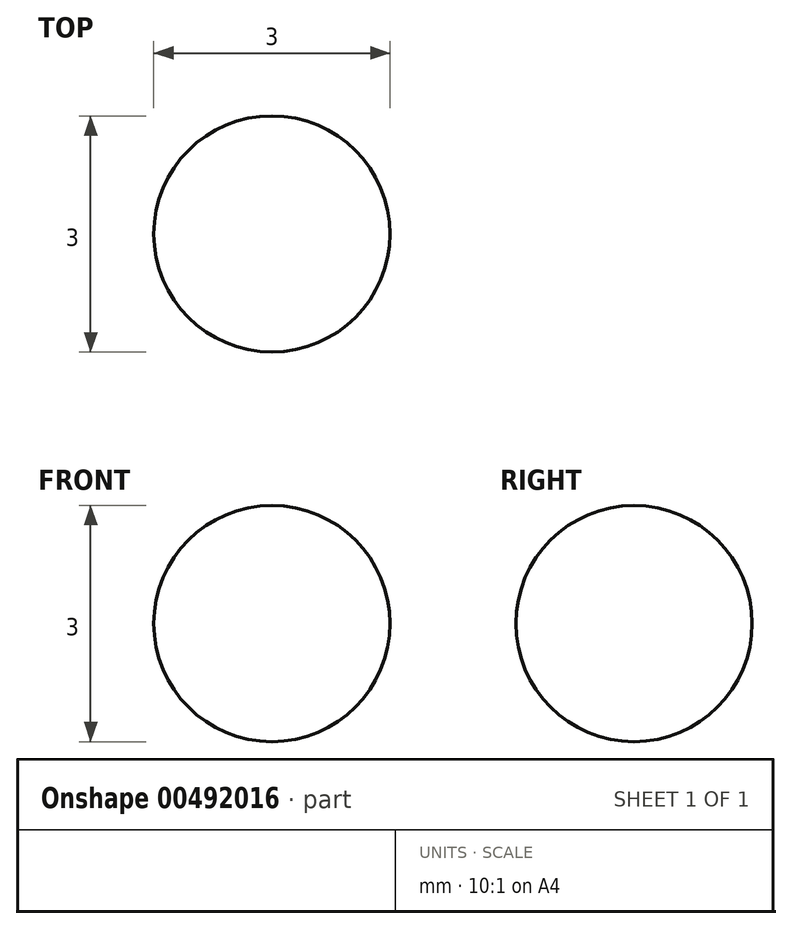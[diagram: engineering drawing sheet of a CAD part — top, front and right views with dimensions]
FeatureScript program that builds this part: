
annotation { "Feature Type Name" : "Feature", "Feature Type Description" : "" }
export const myFeature = defineFeature(function(context is Context, id is Id, definition is map)
    precondition{}
    {
        {
            var Q0;
            Q0=qCreatedBy(makeId("Front.planeOp"),FACE);
            var sketch = newSketch(context, id + "F0", { "sketchPlane" : qUnion([Q0])});
            skArc(sketch, "E0", {"start": v(0, 10) * mm, "mid": v(1.5, 11.5) * mm, "end": v(0, 13) * mm});
            skLineSegment(sketch, "E1", {"start": v(0, 13) * mm, "end": v(0, 10) * mm});
            skSolve(sketch);
        }
        {
            var Q0;
            Q0 = qSketchRegion(id + "F0", true);
            var Q1;
            Q1=sQuery(id+"F0.wireOp",EDGE,"E1");
            revolve(context, id + "F1", {"entities" : qUnion([Q0]), "axis" : qUnion([Q1]), "revolveType" : RevolveType.FULL});
        }
    });
